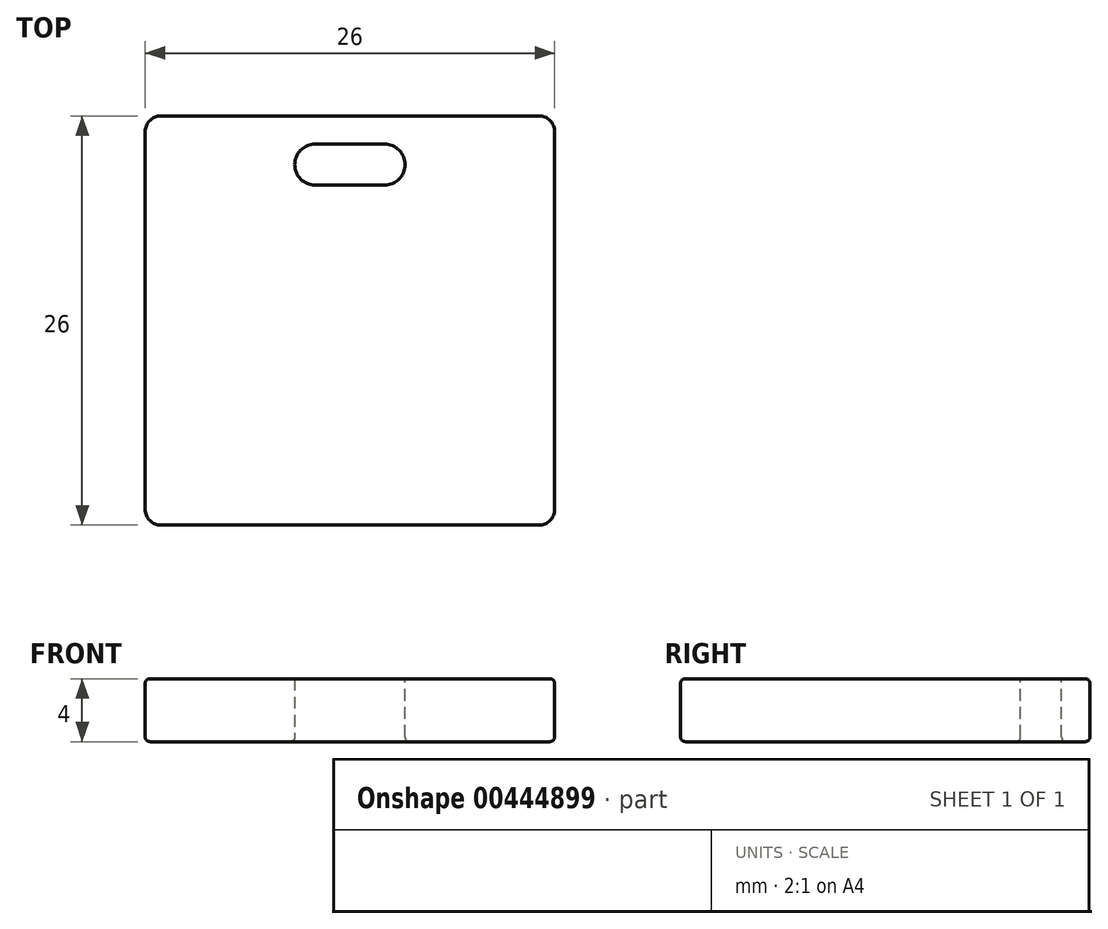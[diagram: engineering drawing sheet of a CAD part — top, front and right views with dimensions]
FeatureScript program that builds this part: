
annotation { "Feature Type Name" : "Feature", "Feature Type Description" : "" }
export const myFeature = defineFeature(function(context is Context, id is Id, definition is map)
    precondition{}
    {
        {
            var Q0;
            Q0=qCreatedBy(makeId("Top.planeOp"),FACE);
            var sketch = newSketch(context, id + "F0", { "sketchPlane" : qUnion([Q0])});
            skLineSegment(sketch, "E0.bottom", {"start": v(-13, 13) * mm, "end": v(13, 13) * mm});
            skLineSegment(sketch, "E0.top", {"start": v(-13, -13) * mm, "end": v(13, -13) * mm});
            skLineSegment(sketch, "E0.left", {"start": v(-13, 13) * mm, "end": v(-13, -13) * mm});
            skLineSegment(sketch, "E0.right", {"start": v(13, 13) * mm, "end": v(13, -13) * mm});
            skPoint(sketch, "E0.middle", {"position": v(0, 0) * mm});
            skSolve(sketch);
        }
        {
            var Q0;
            Q0 = qSketchRegion(id + "F0", true);
            extrude(context, id + "F1", {"entities" : qUnion([Q0]), "depth" : 4 * mm});
        }
        {
            var Q0;
            Q0=makeQuery(id+"F1.opExtrude","SWEPT_EDGE",EDGE,{"disambiguationData":[OSD([sQuery(id+"F0.wireOp",EDGE,"E0.top"),sQuery(id+"F0.wireOp",EDGE,"E0.left")])]});
            var Q1;
            Q1=makeQuery(id+"F1.opExtrude","SWEPT_EDGE",EDGE,{"disambiguationData":[OSD([sQuery(id+"F0.wireOp",EDGE,"E0.bottom"),sQuery(id+"F0.wireOp",EDGE,"E0.left")])]});
            var Q2;
            Q2=makeQuery(id+"F1.opExtrude","SWEPT_EDGE",EDGE,{"disambiguationData":[OSD([sQuery(id+"F0.wireOp",EDGE,"E0.top"),sQuery(id+"F0.wireOp",EDGE,"E0.right")])]});
            var Q3;
            Q3=makeQuery(id+"F1.opExtrude","SWEPT_EDGE",EDGE,{"disambiguationData":[OSD([sQuery(id+"F0.wireOp",EDGE,"E0.bottom"),sQuery(id+"F0.wireOp",EDGE,"E0.right")])]});
            fillet(context, id + "F2", {"entities" : qUnion([Q0, Q1, Q2, Q3]), "radius" : 1 * mm, "tangentPropagation" : true, "allowEdgeOverflow" : false});
        }
        {
            var Q0;
            Q0=makeQuery(id+"F1.opExtrude","CAP_FACE",FACE,{"disambiguationData":[OSD([sQuery(id+"F0.wireOp",EDGE,"E0.bottom"),sQuery(id+"F0.wireOp",EDGE,"E0.top"),sQuery(id+"F0.wireOp",EDGE,"E0.left"),sQuery(id+"F0.wireOp",EDGE,"E0.right")])],"isStart":false});
            var sketch = newSketch(context, id + "F3", { "sketchPlane" : qUnion([Q0])});
            skCircle(sketch, "E1", {"center": v(0, 0) * mm, "radius": 10 * mm});
            skSolve(sketch);
        }
        {
            var Q0;
            Q0=makeQuery(id+"F3.imprint","IMPRINT",FACE,{"disambiguationData":[TD([[makeQuery(id+"F3.imprint","IMPRINT",EDGE,{"derivedFrom":sQuery(id+"F3.wireOp",EDGE,"E1")}),-1.0]])]});
            var sketch = newSketch(context, id + "F4", { "sketchPlane" : qUnion([Q0])});
            skLineSegment(sketch, "E2.bottom", {"start": v(-3.5, 8.6) * mm, "end": v(3.5, 8.6) * mm});
            skLineSegment(sketch, "E2.top", {"start": v(-3.5, 11.2) * mm, "end": v(3.5, 11.2) * mm});
            skLineSegment(sketch, "E2.left", {"start": v(-3.5, 8.6) * mm, "end": v(-3.5, 11.2) * mm});
            skLineSegment(sketch, "E2.right", {"start": v(3.5, 8.6) * mm, "end": v(3.5, 11.2) * mm});
            skPoint(sketch, "E2.middle", {"position": v(0, 9.9) * mm});
            skSolve(sketch);
        }
        {
            var Q0;
            Q0 = qSketchRegion(id + "F4", true);
            extrude(context, id + "F5", {"entities" : qUnion([Q0]), "operationType" : NewBodyOperationType.REMOVE, "oppositeDirection" : true, "depth" : 25 * mm});
        }
        {
            var Q0;
            Q0=makeQuery(id+"F5.boolean.opBoolean","COPY",EDGE,{"derivedFrom":makeQuery(id+"F5.opExtrude","SWEPT_EDGE",EDGE,{"disambiguationData":[OSD([sQuery(id+"F4.wireOp",EDGE,"E2.top"),sQuery(id+"F4.wireOp",EDGE,"E2.left")])]})});
            var Q1;
            Q1=makeQuery(id+"F5.boolean.opBoolean","COPY",EDGE,{"derivedFrom":makeQuery(id+"F5.opExtrude","SWEPT_EDGE",EDGE,{"disambiguationData":[OSD([sQuery(id+"F4.wireOp",EDGE,"E2.top"),sQuery(id+"F4.wireOp",EDGE,"E2.right")])]})});
            var Q2;
            Q2=makeQuery(id+"F5.boolean.opBoolean","COPY",EDGE,{"derivedFrom":makeQuery(id+"F5.opExtrude","SWEPT_EDGE",EDGE,{"disambiguationData":[OSD([sQuery(id+"F4.wireOp",EDGE,"E2.bottom"),sQuery(id+"F4.wireOp",EDGE,"E2.right")])]})});
            var Q3;
            Q3=makeQuery(id+"F5.boolean.opBoolean","COPY",EDGE,{"derivedFrom":makeQuery(id+"F5.opExtrude","SWEPT_EDGE",EDGE,{"disambiguationData":[OSD([sQuery(id+"F4.wireOp",EDGE,"E2.bottom"),sQuery(id+"F4.wireOp",EDGE,"E2.left")])]})});
            fillet(context, id + "F6", {"entities" : qUnion([Q0, Q1, Q2, Q3]), "radius" : 1.3 * mm, "tangentPropagation" : true, "allowEdgeOverflow" : false});
        }
        {
            var Q0;
            Q0=makeQuery(id+"F1.opExtrude","CAP_EDGE",EDGE,{"disambiguationData":[OSD([sQuery(id+"F0.wireOp",EDGE,"E0.left")])],"isStart":false});
            var Q1;
            Q1=makeQuery(id+"F1.opExtrude","CAP_EDGE",EDGE,{"disambiguationData":[OSD([sQuery(id+"F0.wireOp",EDGE,"E0.left")])],"isStart":true});
            var Q2;
            Q2=makeQuery(id+"F5.boolean.opBoolean","COPY",EDGE,{"derivedFrom":makeQuery(id+"F5.opExtrude","CAP_EDGE",EDGE,{"disambiguationData":[OSD([sQuery(id+"F4.wireOp",EDGE,"E2.top")])],"isStart":true})});
            var Q3;
            Q3=makeQuery(id+"F5.boolean.opBoolean","INTERSECT",EDGE,{"derivedFrom":[makeQuery(id+"F1.opExtrude","CAP_FACE",FACE,{"disambiguationData":[OSD([sQuery(id+"F0.wireOp",EDGE,"E0.bottom"),sQuery(id+"F0.wireOp",EDGE,"E0.top"),sQuery(id+"F0.wireOp",EDGE,"E0.left"),sQuery(id+"F0.wireOp",EDGE,"E0.right")])],"isStart":true}),makeQuery(id+"F5.opExtrude","SWEPT_FACE",FACE,{"disambiguationData":[OSD([sQuery(id+"F4.wireOp",EDGE,"E2.top")])]})]});
            fillet(context, id + "F7", {"entities" : qUnion([Q0, Q1, Q2, Q3]), "radius" : 0.3 * mm, "tangentPropagation" : true, "allowEdgeOverflow" : false});
        }
    });
